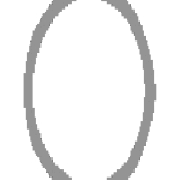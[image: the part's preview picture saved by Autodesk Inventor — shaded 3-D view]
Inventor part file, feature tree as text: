
AUTODESK INVENTOR PART (.ipt)
format: ipt  version: 2021 (Build 250183000, 183)  size: 109,568 bytes
history: native  units: in
note: dims shown in document units (in); Inventor stores cm internally (conversion verified against a paired STEP export)
features: other x4, sketch x3, plane x1
ambient origin geometry x8: Origin, YZ Plane, XZ Plane, XY Plane, X Axis, Y Axis, Z Axis, Center Point
bodies: Solid1 (feature_tree), Body (feature_tree)
feature tree (8):
  other  "Driven Length"
  other  "Frame Generator"
  other  "Start Plane"
  other  "End Plane"
  sketch  "Sketch"  dims[d2=14.4375in d4=-0.0in d5=14.4375in d6=0.12in d7=0.0in d8=90.0deg d9=14.4375in]
  sketch  "Sketch2"  dims[d0=1.0in]
  plane  "Work Plane3"
  sketch  "Sketch3"  dims[d1=0.065in]
